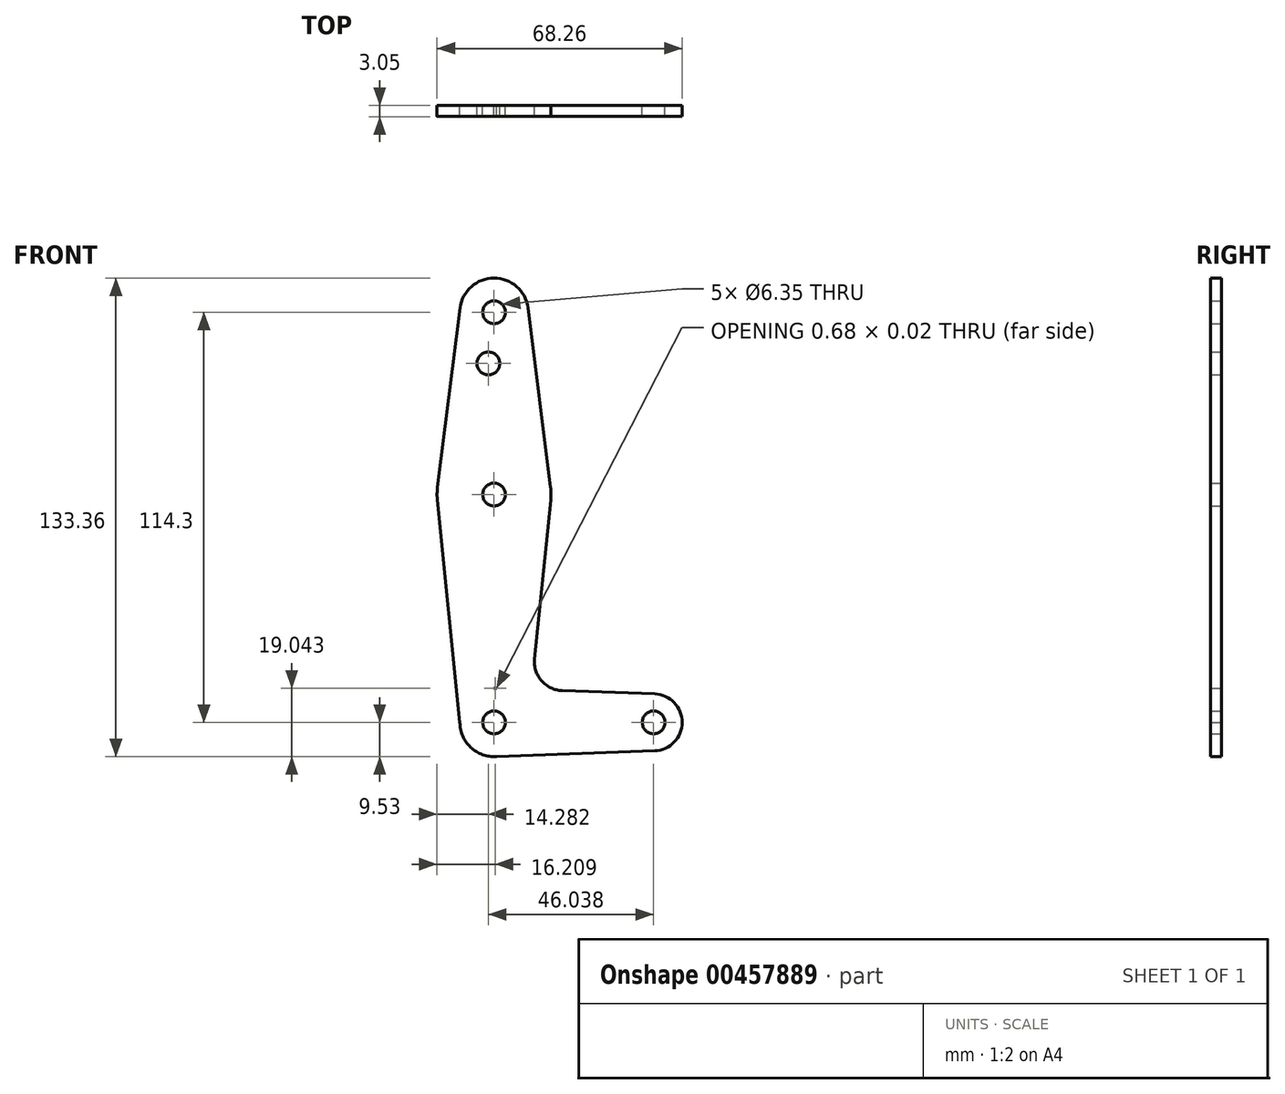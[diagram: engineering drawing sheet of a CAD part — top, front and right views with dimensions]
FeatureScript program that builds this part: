
annotation { "Feature Type Name" : "Feature", "Feature Type Description" : "" }
export const myFeature = defineFeature(function(context is Context, id is Id, definition is map)
    precondition{}
    {
        {
            var Q0;
            Q0=qCreatedBy(makeId("Front.planeOp"),FACE);
            var sketch = newSketch(context, id + "F0", { "sketchPlane" : qUnion([Q0])});
            skLineSegment(sketch, "E0", {"start": v(0, 0) * mm, "end": v(0, 114.3) * mm, "construction": true});
            skLineSegment(sketch, "E1", {"start": v(0, 0) * mm, "end": v(44.45, 0) * mm, "construction": true});
            skCircle(sketch, "E2", {"center": v(0, 114.3) * mm, "radius": 9.53 * mm});
            skCircle(sketch, "E3", {"center": v(44.45, 0) * mm, "radius": 7.94 * mm});
            skCircle(sketch, "E4", {"center": v(0, 0) * mm, "radius": 9.53 * mm});
            skCircle(sketch, "E5", {"center": v(0, 63.5) * mm, "radius": 15.88 * mm});
            skLineSegment(sketch, "E6", {"start": v(11.3, 17.6) * mm, "end": v(15.8, 61.9) * mm});
            skLineSegment(sketch, "E7", {"start": v(-9.45, 115.5) * mm, "end": v(-15.75, 65.48) * mm});
            skCircle(sketch, "E8", {"center": v(-1.59, 100.03) * mm, "radius": 3.18 * mm});
            skCircle(sketch, "E9", {"center": v(0, 0) * mm, "radius": 3.18 * mm});
            skCircle(sketch, "E10", {"center": v(0, 63.5) * mm, "radius": 3.18 * mm});
            skCircle(sketch, "E11", {"center": v(0, 114.3) * mm, "radius": 3.18 * mm});
            skCircle(sketch, "E12", {"center": v(44.45, 0) * mm, "radius": 3.18 * mm});
            skLineSegment(sketch, "E13", {"start": v(0, 9.52) * mm, "end": v(0.68, 9.5) * mm});
            skLineSegment(sketch, "E14", {"start": v(0, -9.52) * mm, "end": v(44.73, -7.93) * mm});
            skLineSegment(sketch, "E15.MirrorCS", {"start": v(9.45, 115.5) * mm, "end": v(15.75, 65.48) * mm});
            skLineSegment(sketch, "E16.MirrorCS", {"start": v(-9.52, 0) * mm, "end": v(-15.8, 61.9) * mm});
            skLineSegment(sketch, "E17.trimOffspring", {"start": v(18.93, 8.85) * mm, "end": v(44.73, 7.93) * mm});
            skPoint(sketch, "E18.orphan", {"position": v(9.52, 0) * mm});
            skPoint(sketch, "E19.visualSharp", {"position": v(10.45, 9.15) * mm});
            skArc(sketch, "E19.filletArc", {"start": v(11.3, 17.6) * mm, "mid": v(13.22, 11.57) * mm, "end": v(18.93, 8.85) * mm});
            skSolve(sketch);
        }
        {
            var Q0;
            Q0 = qSketchRegion(id + "F0", true);
            extrude(context, id + "F1", {"entities" : qUnion([Q0]), "depth" : 3.05 * mm});
        }
    });
